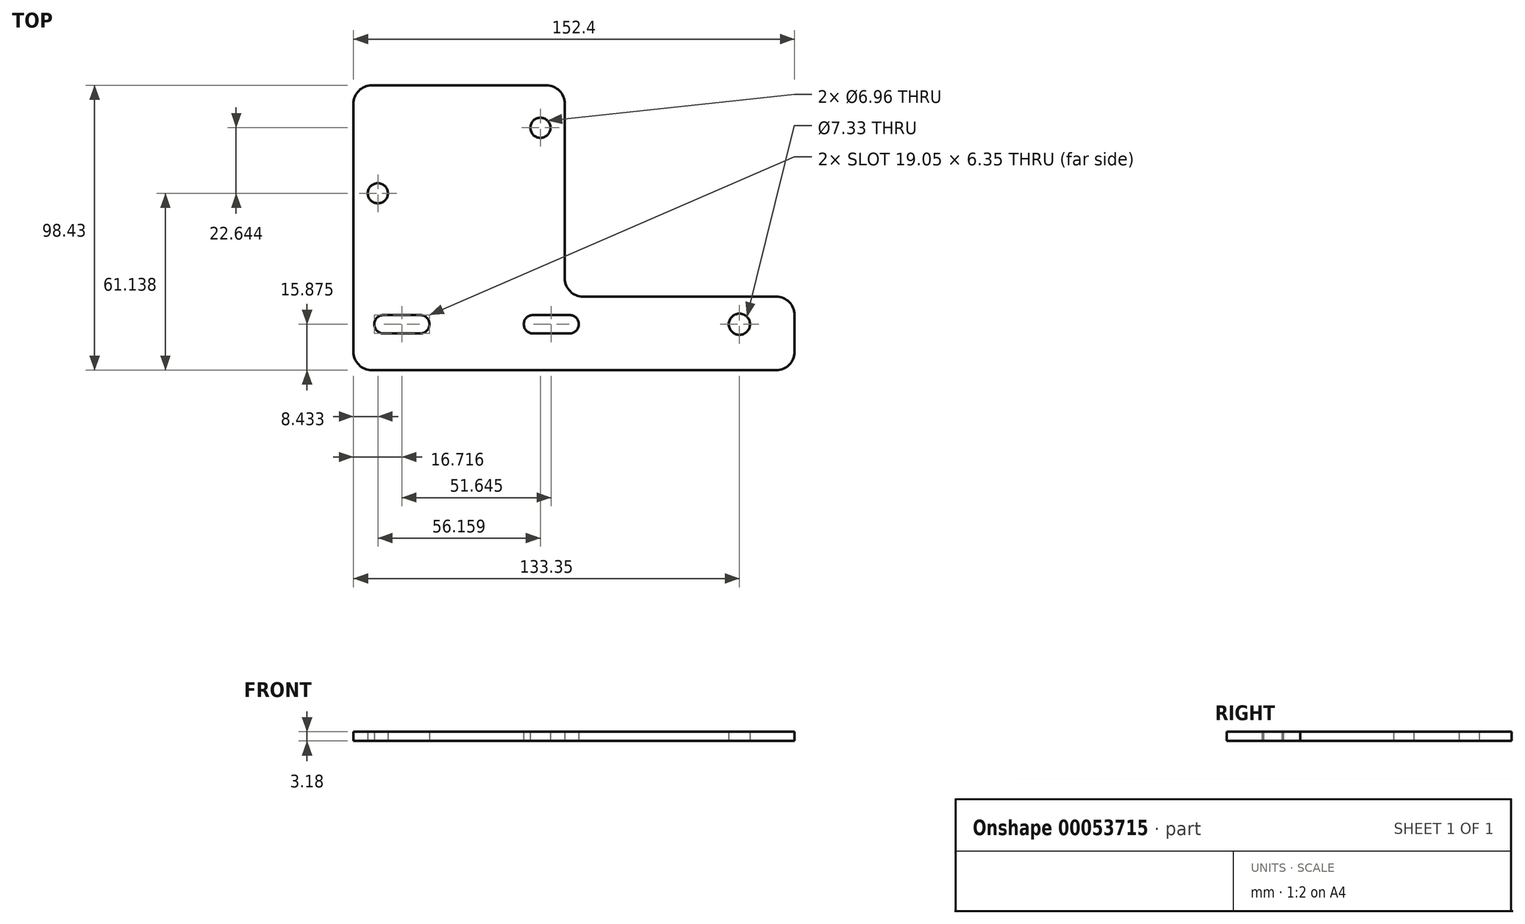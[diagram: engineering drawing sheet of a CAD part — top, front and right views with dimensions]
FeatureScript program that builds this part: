
annotation { "Feature Type Name" : "Feature", "Feature Type Description" : "" }
export const myFeature = defineFeature(function(context is Context, id is Id, definition is map)
    precondition{}
    {
        {
            var Q0;
            Q0=qCreatedBy(makeId("Top.planeOp"),FACE);
            var sketch = newSketch(context, id + "F0", { "sketchPlane" : qUnion([Q0])});
            skLineSegment(sketch, "E0", {"start": v(-82.92, -25.4) * mm, "end": v(56.78, -25.4) * mm});
            skLineSegment(sketch, "E1", {"start": v(63.13, -19.05) * mm, "end": v(63.13, -6.35) * mm});
            skLineSegment(sketch, "E2", {"start": v(56.78, 0) * mm, "end": v(-9.9, 0) * mm});
            skLineSegment(sketch, "E3", {"start": v(-16.24, 6.35) * mm, "end": v(-16.24, 66.67) * mm});
            skLineSegment(sketch, "E4", {"start": v(-22.6, 73.02) * mm, "end": v(-82.92, 73.02) * mm});
            skLineSegment(sketch, "E5", {"start": v(-89.27, 66.67) * mm, "end": v(-89.27, -19.05) * mm});
            skLineSegment(sketch, "E6", {"start": v(-78.9, -9.53) * mm, "end": v(-66.2, -9.53) * mm});
            skLineSegment(sketch, "E7", {"start": v(-27.26, -9.53) * mm, "end": v(-14.56, -9.53) * mm});
            skArc(sketch, "E8.0.startCap", {"start": v(-27.26, -12.7) * mm, "mid": v(-30.43, -9.53) * mm, "end": v(-27.26, -6.35) * mm});
            skArc(sketch, "E8.0.endCap", {"start": v(-14.56, -6.35) * mm, "mid": v(-11.38, -9.53) * mm, "end": v(-14.56, -12.7) * mm});
            skLineSegment(sketch, "E8.0.left", {"start": v(-27.26, -6.35) * mm, "end": v(-14.56, -6.35) * mm});
            skLineSegment(sketch, "E8.0.right", {"start": v(-27.26, -12.7) * mm, "end": v(-14.56, -12.7) * mm});
            skArc(sketch, "E9.0.startCap", {"start": v(-78.9, -12.7) * mm, "mid": v(-82.08, -9.53) * mm, "end": v(-78.9, -6.35) * mm});
            skArc(sketch, "E9.0.endCap", {"start": v(-66.2, -6.35) * mm, "mid": v(-63.03, -9.53) * mm, "end": v(-66.2, -12.7) * mm});
            skLineSegment(sketch, "E9.0.left", {"start": v(-78.9, -6.35) * mm, "end": v(-66.2, -6.35) * mm});
            skLineSegment(sketch, "E9.0.right", {"start": v(-78.9, -12.7) * mm, "end": v(-66.2, -12.7) * mm});
            skCircle(sketch, "E10", {"center": v(44.08, -9.53) * mm, "radius": 3.66 * mm});
            skPoint(sketch, "E11.visualSharp", {"position": v(-16.24, 73.02) * mm});
            skArc(sketch, "E11.filletArc", {"start": v(-16.24, 66.67) * mm, "mid": v(-18.1, 71.17) * mm, "end": v(-22.6, 73.02) * mm});
            skPoint(sketch, "E12.visualSharp", {"position": v(-89.27, 73.02) * mm});
            skArc(sketch, "E12.filletArc", {"start": v(-82.92, 73.02) * mm, "mid": v(-87.41, 71.17) * mm, "end": v(-89.27, 66.67) * mm});
            skPoint(sketch, "E13.visualSharp", {"position": v(-89.27, -25.4) * mm});
            skArc(sketch, "E13.filletArc", {"start": v(-89.27, -19.05) * mm, "mid": v(-87.41, -23.54) * mm, "end": v(-82.92, -25.4) * mm});
            skPoint(sketch, "E14.visualSharp", {"position": v(63.13, 0) * mm});
            skArc(sketch, "E14.filletArc", {"start": v(63.13, -6.35) * mm, "mid": v(61.27, -1.86) * mm, "end": v(56.78, 0) * mm});
            skPoint(sketch, "E15.visualSharp", {"position": v(63.13, -25.4) * mm});
            skArc(sketch, "E15.filletArc", {"start": v(56.78, -25.4) * mm, "mid": v(61.27, -23.54) * mm, "end": v(63.13, -19.05) * mm});
            skPoint(sketch, "E16.visualSharp", {"position": v(-16.24, 0) * mm});
            skArc(sketch, "E16.filletArc", {"start": v(-16.24, 6.35) * mm, "mid": v(-14.39, 1.86) * mm, "end": v(-9.9, 0) * mm});
            skCircle(sketch, "E17", {"center": v(-24.68, 58.38) * mm, "radius": 3.48 * mm});
            skCircle(sketch, "E18", {"center": v(-80.84, 35.74) * mm, "radius": 3.48 * mm});
            skLineSegment(sketch, "E19", {"start": v(-78.9, -9.53) * mm, "end": v(44.08, -9.53) * mm, "construction": true});
            skSolve(sketch);
        }
        {
            var Q0;
            Q0=makeQuery(id+"F0.imprint","IMPRINT",FACE,{"disambiguationData":[TD([[makeQuery(id+"F0.imprint","IMPRINT",EDGE,{"derivedFrom":sQuery(id+"F0.wireOp",EDGE,"E0")}),1.0]])]});
            extrude(context, id + "F1", {"entities" : qUnion([Q0]), "depth" : 3.17 * mm});
        }
    });
